FCSTD DOCUMENT  (FreeCAD 0.19R24366 (Git))
Label: Pi and controller board V1 prototype rear bracket
License: All rights reserved
LicenseURL: http://en.wikipedia.org/wiki/All_rights_reserved
objects: Sketcher::SketchObject×1, PartDesign::Body×1
note: 2 computed .brp shape members not serialized (recipe doc carries the construction recipe); baked Part::Feature solids carry a one-line shape summary decoded from their .brp

FEATURE [Sketcher::SketchObject] Sketch
  FullyConstrained = true
  MapMode = 5
  Support = -> [XY_Plane]
  sketch-geometry (23):
    g0: Circle CenterX=-170 CenterY=0 CenterZ=0 NormalX=0 NormalY=0 NormalZ=1 AngleXU=0 Radius=3
    g1: Circle CenterX=170 CenterY=0 CenterZ=0 NormalX=0 NormalY=0 NormalZ=1 AngleXU=0 Radius=3
    g2: LineSegment StartX=-178 StartY=-10 StartZ=0 EndX=178 EndY=-10 EndZ=0
    g3: LineSegment StartX=180 StartY=-8 StartZ=0 EndX=180 EndY=87 EndZ=0
    g4: LineSegment StartX=178 StartY=89 StartZ=0 EndX=55 EndY=89 EndZ=0
    g5: LineSegment StartX=-180 StartY=87 StartZ=0 EndX=-180 EndY=-8 EndZ=0
    g6: LineSegment StartX=-180 StartY=36 StartZ=0 EndX=180 EndY=36 EndZ=0
    g7: LineSegment StartX=-170 StartY=0 StartZ=0 EndX=-170 EndY=80 EndZ=0
    g8: LineSegment StartX=170 StartY=0 StartZ=0 EndX=170 EndY=80 EndZ=0
    g9: Circle CenterX=-170 CenterY=80 CenterZ=0 NormalX=0 NormalY=0 NormalZ=1 AngleXU=0 Radius=2.5
    g10: Circle CenterX=170 CenterY=80 CenterZ=0 NormalX=0 NormalY=0 NormalZ=1 AngleXU=0 Radius=2.5
    g11: Circle CenterX=0 CenterY=80 CenterZ=0 NormalX=0 NormalY=0 NormalZ=1 AngleXU=0 Radius=2.5
    g12: LineSegment StartX=-170 StartY=80 StartZ=0 EndX=170 EndY=80 EndZ=0
    g13: ArcOfCircle CenterX=-178 CenterY=87 CenterZ=0 NormalX=0 NormalY=0 NormalZ=1 AngleXU=0 Radius=2 StartAngle=1.5708 EndAngle=3.14159
    g14: ArcOfCircle CenterX=-178 CenterY=-8 CenterZ=0 NormalX=0 NormalY=0 NormalZ=1 AngleXU=0 Radius=2 StartAngle=3.14159 EndAngle=4.71239
    g15: ArcOfCircle CenterX=178 CenterY=-8 CenterZ=0 NormalX=0 NormalY=0 NormalZ=1 AngleXU=0 Radius=2 StartAngle=4.71239 EndAngle=6.28319
    g16: ArcOfCircle CenterX=178 CenterY=87 CenterZ=0 NormalX=0 NormalY=0 NormalZ=1 AngleXU=0 Radius=2 StartAngle=3e-15 EndAngle=1.5708
    g17: LineSegment StartX=25 StartY=89 StartZ=0 EndX=25 EndY=71 EndZ=0
    g18: LineSegment StartX=25 StartY=71 StartZ=0 EndX=55 EndY=71 EndZ=0
    g19: LineSegment StartX=55 StartY=71 StartZ=0 EndX=55 EndY=89 EndZ=0
    g20: GeomPoint X=40 Y=71 Z=0
    g21: LineSegment StartX=25 StartY=89 StartZ=0 EndX=-178 EndY=89 EndZ=0
    g22: LineSegment StartX=25 StartY=89 StartZ=0 EndX=55 EndY=89 EndZ=0
  constraints (57):
    c: PointOnObject(g0,g-1)
    c: Symmetric(g0,g1,g-2)
    c: Horizontal(g4)
    c: Vertical(g3)
    c: Vertical(g5)
    c: PointOnObject(g6,g5)
    c: PointOnObject(g6,g3)
    c: Horizontal(g6)
    c: Coincident(g7,g0)
    c: Vertical(g7)
    c: Coincident(g8,g1)
    c: Vertical(g8)
    c: Equal(g7,g8)
    c: Coincident(g9,g7)
    c: Coincident(g10,g8)
    c: PointOnObject(g11,g-2)
    c: Coincident(g12,g7)
    c: Coincident(g12,g8)
    c: Equal(g0,g1)
    c: Equal(g9,g11)
    c: Equal(g11,g10)
    c: Diameter(g9) = 5
    c: Diameter(g0) = 6
    c: DistanceY(g8,g8) = 80
    c: PointOnObject(g11,g12)
    c: Tangent(g5,g13) = -1.5708
    c: Tangent(g2,g14) = -1.5708
    c: Tangent(g5,g14) = -1.5708
    c: Tangent(g3,g15) = -1.5708
    c: Tangent(g2,g15) = -1.5708
    c: Tangent(g4,g16) = -1.5708
    c: Tangent(g3,g16) = -1.5708
    c: Equal(g16,g15)
    c: Equal(g15,g13)
    c: Equal(g13,g14)
    c: Radius(g13) = 2
    c: Horizontal(g2)
    c: DistanceY(g9,g21) = 9
    c: DistanceY(g2,g6) = 46
    c: DistanceX(g1,g3) = 10
    c: DistanceX(g5,g0) = 10
    c: DistanceX(g5,g3) = 360
    c: DistanceY(g2,g0) = 10
    c: Coincident(g18,g17)
    c: Coincident(g19,g18)
    c: Vertical(g19)
    c: Horizontal(g18)
    c: Symmetric(g17,g17,g12)
    c: Symmetric(g17,g18,g20)
    c: DistanceX(g18,g18) = 30
    c: DistanceX(g20,g3) = 140
    c: Coincident(g4,g19)
    c: Coincident(g21,g17)
    c: Tangent(g4,g21)
    c: Coincident(g22,g17)
    c: Coincident(g22,g4)
    c: Tangent(g21,g13) = -1.5708
FEATURE [PartDesign::Body] Body
  Group = -> [Sketch]
  Origin = -> Origin
